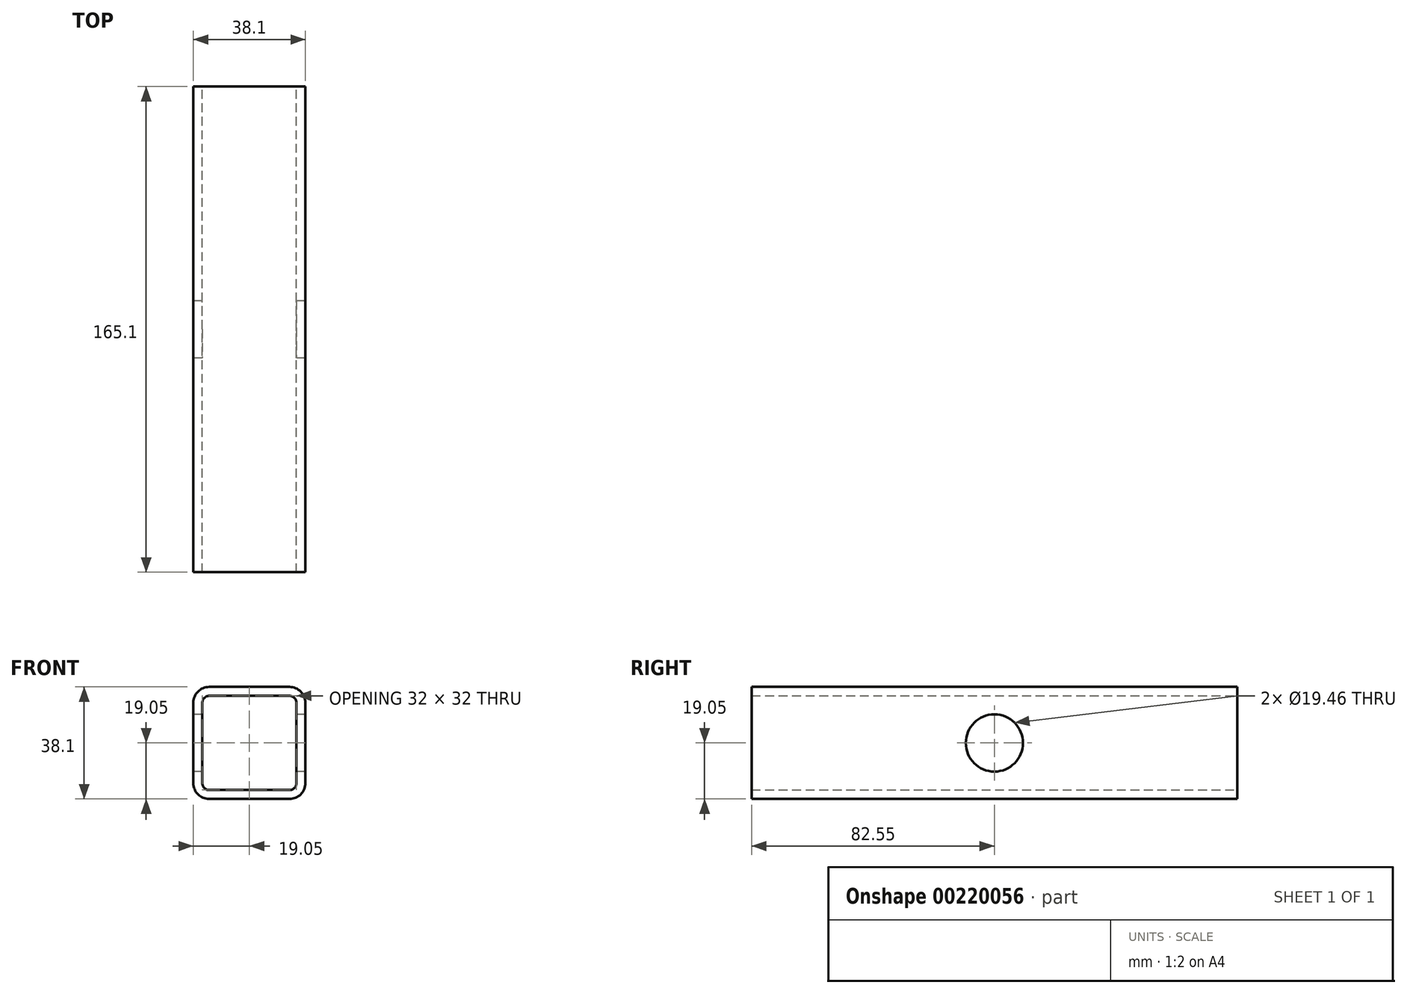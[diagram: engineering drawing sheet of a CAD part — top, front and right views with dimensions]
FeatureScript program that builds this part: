
annotation { "Feature Type Name" : "Feature", "Feature Type Description" : "" }
export const myFeature = defineFeature(function(context is Context, id is Id, definition is map)
    precondition{}
    {
        {
            var Q0;
            Q0=qCreatedBy(makeId("Front.planeOp"),FACE);
            var sketch = newSketch(context, id + "F0", { "sketchPlane" : qUnion([Q0])});
            skLineSegment(sketch, "E0.bottom", {"start": v(13.67, 19.05) * mm, "end": v(-13.67, 19.05) * mm});
            skLineSegment(sketch, "E0.top", {"start": v(13.67, -19.05) * mm, "end": v(-13.67, -19.05) * mm});
            skLineSegment(sketch, "E0.left", {"start": v(19.05, 13.67) * mm, "end": v(19.05, -13.67) * mm});
            skLineSegment(sketch, "E0.right", {"start": v(-19.05, 13.67) * mm, "end": v(-19.05, -13.67) * mm});
            skPoint(sketch, "E0.middle", {"position": v(0, 0) * mm});
            skLineSegment(sketch, "E1.bottom", {"start": v(13.67, 16) * mm, "end": v(-13.67, 16) * mm});
            skLineSegment(sketch, "E1.top", {"start": v(13.67, -16) * mm, "end": v(-13.67, -16) * mm});
            skLineSegment(sketch, "E1.left", {"start": v(16, 13.67) * mm, "end": v(16, -13.67) * mm});
            skLineSegment(sketch, "E1.right", {"start": v(-16, 13.67) * mm, "end": v(-16, -13.67) * mm});
            skPoint(sketch, "E2.visualSharp", {"position": v(-19.05, 19.05) * mm});
            skArc(sketch, "E2.filletArc", {"start": v(-13.67, 19.05) * mm, "mid": v(-17.47, 17.47) * mm, "end": v(-19.05, 13.67) * mm});
            skPoint(sketch, "E3.visualSharp", {"position": v(-16, 16) * mm});
            skArc(sketch, "E3.filletArc", {"start": v(-13.67, 16) * mm, "mid": v(-15.32, 15.32) * mm, "end": v(-16, 13.67) * mm});
            skPoint(sketch, "E4.visualSharp", {"position": v(16, 16) * mm});
            skArc(sketch, "E4.filletArc", {"start": v(16, 13.67) * mm, "mid": v(15.32, 15.32) * mm, "end": v(13.67, 16) * mm});
            skPoint(sketch, "E5.visualSharp", {"position": v(16, -16) * mm});
            skArc(sketch, "E5.filletArc", {"start": v(13.67, -16) * mm, "mid": v(15.32, -15.32) * mm, "end": v(16, -13.67) * mm});
            skPoint(sketch, "E6.visualSharp", {"position": v(-16, -16) * mm});
            skArc(sketch, "E6.filletArc", {"start": v(-16, -13.67) * mm, "mid": v(-15.32, -15.32) * mm, "end": v(-13.67, -16) * mm});
            skPoint(sketch, "E7.visualSharp", {"position": v(19.05, 19.05) * mm});
            skArc(sketch, "E7.filletArc", {"start": v(19.05, 13.67) * mm, "mid": v(17.47, 17.47) * mm, "end": v(13.67, 19.05) * mm});
            skPoint(sketch, "E8.visualSharp", {"position": v(19.05, -19.05) * mm});
            skArc(sketch, "E8.filletArc", {"start": v(13.67, -19.05) * mm, "mid": v(17.47, -17.47) * mm, "end": v(19.05, -13.67) * mm});
            skPoint(sketch, "E9.visualSharp", {"position": v(-19.05, -19.05) * mm});
            skArc(sketch, "E9.filletArc", {"start": v(-19.05, -13.67) * mm, "mid": v(-17.47, -17.47) * mm, "end": v(-13.67, -19.05) * mm});
            skSolve(sketch);
        }
        {
            var Q0;
            Q0 = qSketchRegion(id + "F0", true);
            extrude(context, id + "F1", {"entities" : qUnion([Q0]), "endBound" : BoundingType.SYMMETRIC, "depth" : 165.1 * mm});
        }
        {
            var Q0;
            Q0=makeQuery(id+"F1.opExtrude","SWEPT_FACE",FACE,{"disambiguationData":[OSD([sQuery(id+"F0.wireOp",EDGE,"E0.right")])]});
            var sketch = newSketch(context, id + "F2", { "sketchPlane" : qUnion([Q0])});
            skCircle(sketch, "E10", {"center": v(0, 0) * mm, "radius": 9.73 * mm});
            skSolve(sketch);
        }
        {
            var Q0;
            Q0 = qSketchRegion(id + "F2", true);
            extrude(context, id + "F3", {"entities" : qUnion([Q0]), "operationType" : NewBodyOperationType.REMOVE, "endBound" : BoundingType.THROUGH_ALL, "oppositeDirection" : true, "depth" : 25.4 * mm});
        }
    });
